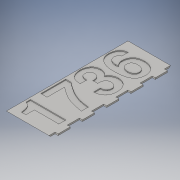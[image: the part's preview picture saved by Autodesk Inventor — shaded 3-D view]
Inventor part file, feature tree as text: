
AUTODESK INVENTOR PART (.ipt)
format: ipt  version: 2016 (Build 200138000, 138)  size: 244,224 bytes
history: native  units: in
note: dims shown in document units (in); Inventor stores cm internally (conversion verified against a paired STEP export)
features: extrude x3, sketch x3, chamfer x1
ambient origin geometry x8: Origin, YZ Plane, XZ Plane, XY Plane, X Axis, Y Axis, Z Axis, Center Point
bodies: Solid1 (feature_tree)
feature tree (7):
  extrude  "Extrusion1"  Depth=10.0in
  extrude  "Extrusion2"  Depth=1.9685in
  chamfer  "Chamfer1"  Distance=0.125in
  sketch  "Sketch1"  dims[d0=3.5in d1=10.0in]
  sketch  "Sketch3"  dims[d2=0.125in d3=0.0in d4=1.9685in d6=2.0in d7=0.3937in d9=1.0in d11=0.125in d12=0.0in]
  sketch  "Sketch4"  dims[d14=0.0in d15=0.075in d16=0.125in d17=0.125in d18=45.0deg]
  extrude  "Extrusion3"  Depth=0.125in TaperAngle=45.0deg
